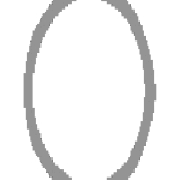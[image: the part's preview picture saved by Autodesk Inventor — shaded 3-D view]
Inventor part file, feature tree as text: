
AUTODESK INVENTOR PART (.ipt)
format: ipt  version: 2021 (Build 250183000, 183)  size: 117,248 bytes
history: native  units: in
note: dims shown in document units (in); Inventor stores cm internally (conversion verified against a paired STEP export)
features: other x4, sketch x3, plane x1
ambient origin geometry x8: Origin, YZ Plane, XZ Plane, XY Plane, X Axis, Y Axis, Z Axis, Center Point
bodies: Solid1 (feature_tree), Body (feature_tree)
feature tree (8):
  other  "Driven Length"
  other  "Frame Generator"
  other  "Start Plane"
  other  "End Plane"
  sketch  "Sketch"  dims[d2=1.5435in d4=-0.0in d5=1.5435in d6=0.12in d7=0.0in d8=90.0deg d9=1.5435in]
  sketch  "Sketch2"  dims[d0=1.0in]
  plane  "Work Plane3"
  sketch  "Sketch3"  dims[d1=0.065in]
